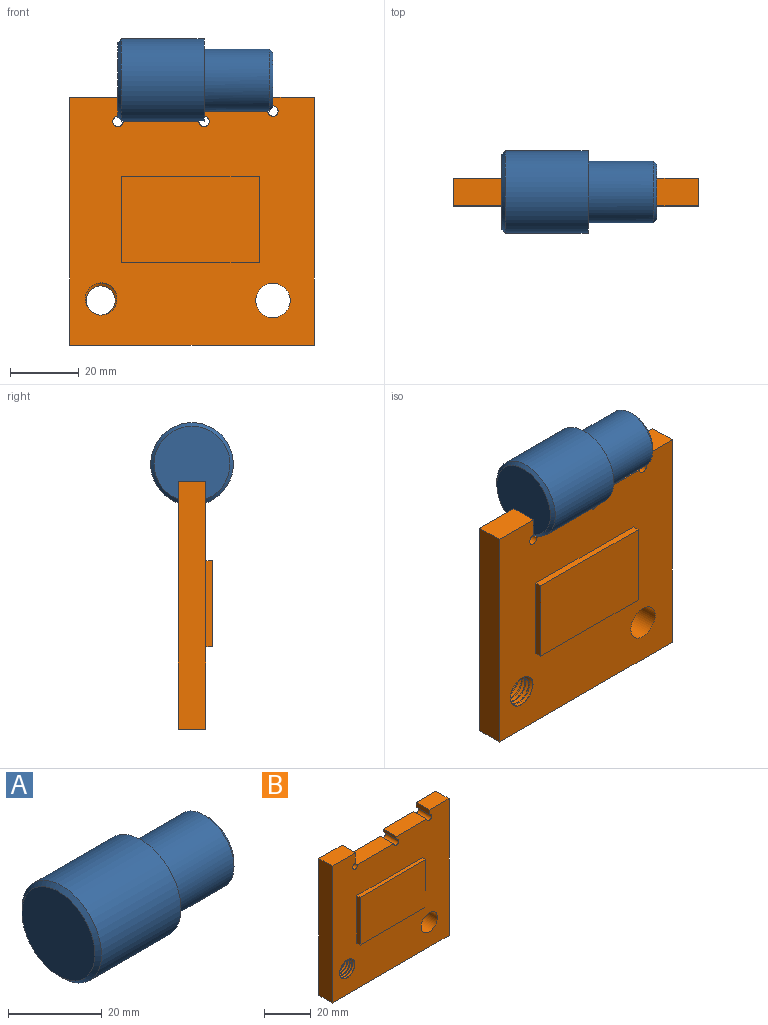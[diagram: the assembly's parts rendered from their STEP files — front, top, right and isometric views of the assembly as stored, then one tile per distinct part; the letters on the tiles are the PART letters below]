
ASSEMBLY  parts=2 mates=1
PART A: 7 faces, bbox 45x24x24 mm
  f0: plane 16x16mm, normal (1,0,0), area 201.1mm2, adj f5
  f1: cylinder r=9mm len=19mm, axis (-1,0,0), area 1074.4mm2, adj f2,f5
  f2: plane 24x24mm, normal (1,0,0), area 197.9mm2, adj f1,f3
  f3: cylinder r=12mm len=24mm, axis (-1,0,0), area 1809.6mm2, adj f2,f6
  f4: plane 22x22mm, normal (-1,0,0), area 380.1mm2, adj f6
  f5: cone r=9mm half-angle=45deg, axis (-1,0,0), area 75.5mm2, adj f0,f1
  f6: cone r=11mm half-angle=45deg, axis (1,0,0), area 102.2mm2, adj f3,f4
PART B: 25 faces, bbox 71.4x11x72.4 mm
  f0: plane 8x1.5mm, normal (-1,0,0), area 12mm2, adj f1,f13,f14,f15
  f1: cylinder r=1.5mm len=8mm, axis (0,1,0), area 56.5mm2, adj f0,f2,f14,f15
  f2: plane 22x8mm, normal (0,0,1), area 176mm2, adj f1,f3,f14,f15
  f3: cylinder r=1.5mm len=8mm, axis (0,1,0), area 56.5mm2, adj f2,f4,f14,f15
  f4: plane 8x5.5mm, normal (1,0,0), area 44mm2, adj f3,f5,f14,f15
  f5: plane 14x8mm, normal (0,0,1), area 112mm2, adj f4,f6,f14,f15
  f6: plane 72x8mm, normal (-1,0,0), area 576mm2, adj f5,f7,f14,f15
  f7: plane 71x8mm, normal (0,0,-1), area 568mm2, adj f6,f8,f14,f15
  f8: plane 72x8mm, normal (1,0,0), area 576mm2, adj f7,f9,f14,f15
  f9: plane 12x8mm, normal (0,0,1), area 96mm2, adj f8,f10,f14,f15
  f10: plane 8x2.5mm, normal (-1,0,0), area 20mm2, adj f9,f11,f14,f15
  f11: cylinder r=1.5mm len=8mm, axis (0,1,0), area 56.5mm2, adj f10,f13,f14,f15
  f12: cylinder r=5mm len=10mm, axis (0,1,0), area 251.3mm2, adj f14,f15
  f13: plane 18.5x8mm, normal (0,0,1), area 148mm2, adj f0,f11,f14,f15
  f14: plane 72.44x71.44mm, normal (0,-1,0), area 3695.5mm2, adj f0,f1,f2,f3,f4,f5,f6,f7
  f15: plane 72.44x71.44mm, normal (0,1,0), area 4695.5mm2, adj f0,f1,f2,f3,f4,f5,f6,f7
  f16: plane 25x2mm, normal (-1,0,0), area 50mm2, adj f14,f17,f19,f20
  f17: plane 40x2mm, normal (0,0,-1), area 80mm2, adj f14,f16,f18,f20
  f18: plane 25x2mm, normal (1,0,0), area 50mm2, adj f14,f17,f19,f20
  f19: plane 40x2mm, normal (0,0,1), area 80mm2, adj f14,f16,f18,f20
  f20: plane 40x25mm, normal (0,-1,0), area 1000mm2, adj f16,f17,f18,f19
  f21: bspline ~11.69x10.12mm, area 146.5mm2, adj f14,f15,f23,f24
  f22: bspline ~11.69x10.12mm, area 146.4mm2, adj f14,f15,f23,f24
  f23: bspline ~11.85x10.26mm, area 37.1mm2, adj f14,f15,f21,f22
  f24: cylinder r=4.25mm len=8.5mm, axis (0,-1,0), area 51.7mm2, adj f14,f15,f21,f22
PLACE A t=(-11.3,-0.61,84.51)mm
PLACE B t=(-25.3,3.39,7.51)mm fixed
MATE fastened B.f4 <-> A.f1  axis (1,0,0) through (-11.3,-0.61,84.51)mm
